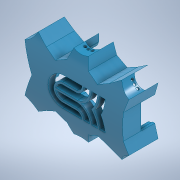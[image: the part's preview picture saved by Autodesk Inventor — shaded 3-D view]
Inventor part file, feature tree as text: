
AUTODESK INVENTOR PART (.ipt)
format: ipt  version: 2020 (Build 240168000, 168)  size: 3,561,472 bytes
history: native  units: mm
features: projected_geometry x120, extrude x44, sketch x44, reference x22, other x20, chamfer x7, hole x3, plane x2
ambient origin geometry x8: Origin, YZ Plane, XZ Plane, XY Plane, X Axis, Y Axis, Z Axis, Center Point
bodies: Solid1 (feature_tree)
feature tree (262):
  extrude  "Extrusion1"  Depth=4.404mm
  extrude  "Extrusion2"  Depth=22.0mm
  extrude  "Extrusion3"  Depth=35.3mm
  hole  "Hole2"  [1 undecoded]
  extrude  "Extrusion10"  Depth=19.0mm
  extrude  "Extrusion15"  Depth=10.0mm
  extrude  "Extrusion17"  Depth=100.0mm
  sketch  "Sketch27"  dims[d14=30.0mm d15=17.453293mm]
  hole  "Hole4"  [1 undecoded]
  extrude  "Extrusion27"  Depth=13.962634mm
  extrude  "Extrusion29"  Depth=4.8mm
  extrude  "Extrusion30"  Depth=6.2mm
  extrude  "Extrusion31"  Depth=2.5mm
  extrude  "Extrusion34"  Depth=2.5mm
  extrude  "Extrusion35"  Depth=2.0mm
  sketch  "Sketch37"  dims[d28=90.0deg d29=6.2mm]
  extrude  "Extrusion36"  Depth=6.2mm
  extrude  "Extrusion37"  Depth=33.0mm
  extrude  "Extrusion38"  Depth=2.5mm
  extrude  "Extrusion39"  Depth=4.8mm
  extrude  "Extrusion40"  Depth=6.2mm
  extrude  "Extrusion41"  Depth=2.5mm
  plane  "Work Plane1"
  extrude  "Extrusion42"  Depth=2.5mm
  hole  "Hole6"  [1 undecoded]
  extrude  "Extrusion43"  Depth=19.402mm
  chamfer  "Chamfer12"  Distance=10.0mm
  extrude  "Extrusion46"  Depth=113.583126mm
  extrude  "Extrusion47"  Depth=235.691804mm
  extrude  "Extrusion48"  Depth=12.4mm
  extrude  "Extrusion49"  Depth=12.4mm
  extrude  "Extrusion50"  Depth=142.600153mm
  extrude  "Extrusion51"  Depth=142.600153mm
  extrude  "Extrusion52"  Depth=35.0mm TaperAngle=0.0deg
  chamfer  "Chamfer13"  Distance=5.0mm
  chamfer  "Chamfer14"  Distance=22.5mm
  chamfer  "Chamfer15"  Distance=45.0mm
  chamfer  "Chamfer16"  Distance=25.0mm
  chamfer  "Chamfer17"  Distance=4.3mm
  chamfer  "Chamfer18"  Distance=9.0mm
  extrude  "Extrusion53"  Depth=35.0mm
  extrude  "Extrusion54"  Depth=35.0mm
  extrude  "Extrusion55"  Depth=35.0mm
  extrude  "Extrusion56"  Depth=35.0mm
  plane  "Work Plane2"
  extrude  "Extrusion57"  Depth=35.0mm
  extrude  "Extrusion58"  Depth=35.0mm TaperAngle=0.0deg
  extrude  "Extrusion59"  Depth=35.0mm
  extrude  "Extrusion60"  Depth=35.0mm
  extrude  "Extrusion61"  Depth=35.0mm
  extrude  "Extrusion62"  Depth=35.0mm
  extrude  "Extrusion66"  Depth=35.0mm
  extrude  "Extrusion67"  Depth=35.0mm
  extrude  "Extrusion68"  Depth=35.0mm
  extrude  "Extrusion69"  Depth=35.0mm
  extrude  "Extrusion70"  Depth=35.0mm
  extrude  "Extrusion71"  Depth=35.0mm
  extrude  "Extrusion72"  Depth=35.0mm
  sketch  "Sketch1"  dims[d0=50.0mm d1=4.404mm]
  reference  "Reference1"
  reference  "Reference2"
  reference  "Reference3"
  reference  "Reference4"
  sketch  "Sketch2"  dims[d2=135.0deg d3=22.0mm]
  reference  "Reference5"
  reference  "Reference6"
  reference  "Reference7"
  reference  "Reference8"
  reference  "Reference9"
  reference  "Reference10"
  reference  "Reference11"
  reference  "Reference12"
  reference  "Reference13"
  reference  "Reference14"
  reference  "Reference15"
  reference  "Reference16"
  sketch  "Sketch3"  dims[d4=35.3mm d5=35.3mm]
  projected_geometry  "Projected Loop1"
  projected_geometry  "Projected Loop2"
  sketch  "Sketch6"  dims[d6=98.287843mm d7=10.0mm]
  reference  "Reference23"
  reference  "Reference24"
  reference  "Reference25"
  reference  "Reference26"
  reference  "Reference27"
  reference  "Reference28"
  sketch  "Sketch13"  dims[d8=19.0mm d9=19.0mm]
  sketch  "Sketch16"  dims[d10=6.0mm d11=10.0mm]
  sketch  "Sketch18"  dims[d12=19.0mm d13=100.0mm]
  projected_geometry  "Projected Loop13"
  projected_geometry  "Projected Loop19"
  projected_geometry  "Projected Loop23"
  projected_geometry  "Projected Loop28"
  projected_geometry  "Projected Loop29"
  projected_geometry  "Projected Loop30"
  sketch  "Sketch28"  dims[d16=30.0mm d17=13.962634mm]
  projected_geometry  "Projected Loop31"
  sketch  "Sketch30"  dims[d18=2.0mm d19=4.8mm]
  projected_geometry  "Projected Loop33"
  sketch  "Sketch31"  dims[d20=6.2mm d21=6.2mm]
  projected_geometry  "Projected Loop34"
  sketch  "Sketch32"  dims[d22=33.0mm d23=2.5mm]
  projected_geometry  "Projected Loop35"
  projected_geometry  "Projected Loop36"
  projected_geometry  "Projected Loop37"
  projected_geometry  "Projected Loop38"
  projected_geometry  "Projected Loop39"
  projected_geometry  "Projected Loop40"
  projected_geometry  "Projected Loop41"
  projected_geometry  "Projected Loop42"
  projected_geometry  "Projected Loop43"
  projected_geometry  "Projected Loop44"
  projected_geometry  "Projected Loop45"
  projected_geometry  "Projected Loop46"
  sketch  "Sketch35"  dims[d24=2.0mm d25=2.5mm]
  projected_geometry  "Projected Loop52"
  sketch  "Sketch36"  dims[d26=2.0mm d27=2.0mm]
  projected_geometry  "Projected Loop53"
  projected_geometry  "Projected Loop54"
  projected_geometry  "Projected Loop55"
  projected_geometry  "Projected Loop56"
  projected_geometry  "Projected Loop57"
  sketch  "Sketch38"  dims[d30=6.2mm d31=33.0mm]
  projected_geometry  "Projected Loop58"
  sketch  "Sketch40"  dims[d32=2.0mm d33=2.5mm]
  projected_geometry  "Projected Loop59"
  sketch  "Sketch41"  dims[d35=2.0mm d36=4.8mm]
  projected_geometry  "Projected Loop60"
  sketch  "Sketch42"  dims[d37=6.2mm d38=6.2mm]
  projected_geometry  "Projected Loop61"
  projected_geometry  "Projected Loop62"
  sketch  "Sketch43"  dims[d39=33.0mm d40=2.5mm]
  projected_geometry  "Projected Loop63"
  sketch  "Sketch46"  dims[d41=2.0mm d42=2.5mm]
  sketch  "Sketch47"  dims[d43=2.0mm d44=2.0mm]
  projected_geometry  "Projected Loop67"
  sketch  "Sketch48"  dims[d45=2.5mm d46=19.402mm]
  projected_geometry  "Projected Loop68"
  sketch  "Sketch49"  dims[d47=169.440339mm]
  projected_geometry  "Projected Loop69"
  sketch  "Sketch50"  dims[d48=155.440339mm]
  projected_geometry  "Projected Loop70"
  sketch  "Sketch51"  dims[d58=2.0mm]
  projected_geometry  "Projected Loop71"
  sketch  "Sketch52"  dims[d59=2.0mm]
  projected_geometry  "Projected Loop72"
  sketch  "Sketch53"  dims[d71=4.8mm]
  projected_geometry  "Projected Loop73"
  sketch  "Sketch54"  dims[d72=33.0mm]
  sketch  "Sketch55"  dims[d73=2.5mm]
  projected_geometry  "Projected Loop74"
  sketch  "Sketch56"  dims[d74=2.0mm]
  projected_geometry  "Projected Loop75"
  projected_geometry  "Projected Loop76"
  projected_geometry  "Projected Loop77"
  projected_geometry  "Projected Loop78"
  projected_geometry  "Projected Loop79"
  projected_geometry  "Projected Loop80"
  sketch  "Sketch58"  dims[d75=2.5mm]
  sketch  "Sketch61"  dims[d76=2.0mm]
  projected_geometry  "Projected Loop91"
  projected_geometry  "Projected Loop92"
  sketch  "Sketch62"  dims[d77=14.0mm]
  projected_geometry  "Projected Loop93"
  sketch  "Sketch63"  dims[d78=2.0mm]
  projected_geometry  "Projected Loop94"
  projected_geometry  "Projected Loop95"
  projected_geometry  "Projected Loop96"
  projected_geometry  "Projected Loop97"
  projected_geometry  "Projected Loop98"
  projected_geometry  "Projected Loop99"
  projected_geometry  "Projected Loop100"
  projected_geometry  "Projected Loop101"
  projected_geometry  "Projected Loop102"
  projected_geometry  "Projected Loop103"
  projected_geometry  "Projected Loop104"
  projected_geometry  "Projected Loop105"
  projected_geometry  "Projected Loop106"
  projected_geometry  "Projected Loop107"
  projected_geometry  "Projected Loop108"
  projected_geometry  "Projected Loop109"
  projected_geometry  "Projected Loop110"
  projected_geometry  "Projected Loop111"
  projected_geometry  "Projected Loop112"
  projected_geometry  "Projected Loop113"
  projected_geometry  "Projected Loop114"
  projected_geometry  "Projected Loop115"
  projected_geometry  "Projected Loop116"
  projected_geometry  "Projected Loop117"
  projected_geometry  "Projected Loop118"
  projected_geometry  "Projected Loop119"
  projected_geometry  "Projected Loop120"
  projected_geometry  "Projected Loop121"
  projected_geometry  "Projected Loop122"
  projected_geometry  "Projected Loop123"
  projected_geometry  "Projected Loop124"
  projected_geometry  "Projected Loop125"
  projected_geometry  "Projected Loop126"
  projected_geometry  "Projected Loop127"
  projected_geometry  "Projected Loop128"
  projected_geometry  "Projected Loop129"
  projected_geometry  "Projected Loop130"
  projected_geometry  "Projected Loop131"
  projected_geometry  "Projected Loop132"
  projected_geometry  "Projected Loop133"
  projected_geometry  "Projected Loop134"
  projected_geometry  "Projected Loop135"
  projected_geometry  "Projected Loop136"
  projected_geometry  "Projected Loop137"
  projected_geometry  "Projected Loop138"
  projected_geometry  "Projected Loop139"
  projected_geometry  "Projected Loop140"
  projected_geometry  "Projected Loop141"
  projected_geometry  "Projected Loop142"
  projected_geometry  "Projected Loop143"
  projected_geometry  "Projected Loop144"
  projected_geometry  "Projected Loop145"
  projected_geometry  "Projected Loop146"
  projected_geometry  "Projected Loop147"
  sketch  "Sketch66"  dims[d79=106.731156mm]
  sketch  "Sketch67"  dims[d80=94.331156mm d81=10.0mm d82=0.0mm]
  projected_geometry  "Projected Loop149"
  sketch  "Sketch71"  dims[d83=146.583126mm d84=113.583126mm]
  projected_geometry  "Projected Loop158"
  sketch  "Sketch72"  dims[d85=207.691804mm d86=235.691804mm]
  projected_geometry  "Projected Loop159"
  sketch  "Sketch73"  dims[d87=89.108678mm d88=12.4mm]
  projected_geometry  "Projected Loop160"
  sketch  "Sketch74"  dims[d89=56.108678mm d90=12.4mm]
  projected_geometry  "Projected Loop161"
  sketch  "Sketch75"  dims[d91=23.0mm d92=142.600153mm]
  projected_geometry  "Projected Loop162"
  sketch  "Sketch76"  dims[d93=170.600153mm d94=142.600153mm]
  projected_geometry  "Projected Loop163"
  sketch  "Sketch77"  dims[d95=19.0mm d96=0.0mm d97=5.0mm d98=0.0mm d153=10.0mm d154=6.0mm d155=4.0mm d156=2.0mm d157=90.0deg d158=3.8mm d159=0.0mm d207=5.0mm d208=22.5mm d209=45.0mm d210=25.0mm d211=0.0mm d253=2.5mm d254=20.0mm d255=9.0mm d256=10.0mm d257=16.0mm d258=27.0mm d259=16.0mm d260=0.3mm d261=0.3mm d262=1.5mm d263=1.5mm d264=2.0mm d265=1.5mm d266=1.5mm d267=2.0mm d268=1.5mm d269=1.5mm d270=2.0mm d271=1.5mm d272=1.5mm d273=2.0mm d274=10.5mm d275=1.75mm d276=3.5mm d277=180.0deg d278=7.0mm d279=0.3mm d280=0.3mm d281=0.3mm d282=0.3mm d283=1.0mm d284=4.3mm d285=0.0mm d310=9.0mm d311=0.0mm d382=3.0mm d383=6.0mm d384=4.0mm d385=2.0mm d386=90.0deg d387=24.0mm d388=0.0mm d396=3.2505mm d397=3.2505mm d398=3.2505mm d400=3.2505mm d401=3.2505mm d402=2.4mm d403=0.0mm d416=3.1mm d455=6.0mm d456=4.5mm d457=4.5mm d458=1.7mm d459=12.4mm d460=6.0mm d461=4.5mm d462=4.5mm d463=6.0mm d464=4.5mm d465=4.5mm d466=6.0mm d467=4.5mm d468=4.5mm d472=6.0mm d473=4.5mm d474=4.5mm d475=4.5mm d476=4.5mm d477=6.0mm d478=154.585126mm d479=147.583126mm d480=147.583126mm d481=9.0mm d482=0.0mm d483=154.585126mm d484=90.108678mm d485=10.7mm d486=147.583126mm d487=66.300077mm d488=72.372447mm d489=10.0mm d490=0.0mm d491=0.0mm d492=231.691804mm d493=91.808678mm d494=139.883126mm d495=171.600153mm d496=1.7mm d497=5.0mm d498=0.0mm d523=88.2mm d524=34.2mm d525=17.1mm d526=44.1mm d527=5.0mm d528=5.0mm d529=10.0mm d530=0.0mm d531=54.9mm d532=27.9mm d533=13.95mm d534=27.45mm d535=2.05mm d536=2.05mm d537=6.0mm d538=6.0mm d539=6.0mm d540=6.0mm d541=10.0mm d542=25.0mm d543=0.0mm d544=18.9mm d545=6.0mm d546=18.9mm d547=6.0mm d548=18.9mm d549=6.0mm d550=18.9mm d551=10.0mm d552=0.0mm d553=48.2mm d554=11.9mm d555=2.5mm d556=1.3mm d557=23.8mm d558=20.0mm d559=0.0mm d560=3.1mm d561=3.1mm d562=3.1mm d563=3.1mm d564=2.4mm d565=0.0mm d566=3.0mm d567=3.0mm d568=3.0mm d569=3.0mm d570=3.0mm d571=3.0mm d572=3.0mm d575=3.0mm d576=3.0mm d577=3.0mm d578=100.0mm d579=0.0mm d580=3.1mm d581=3.1mm d582=3.1mm d583=3.1mm d584=2.4mm d585=0.0mm d586=0.15mm d587=0.15mm d588=20.0mm d589=0.0mm d590=8.0mm d591=0.0mm d592=3.0mm d593=6.0mm d594=4.0mm d595=2.0mm d596=90.0deg d597=6.5mm d598=0.0mm d599=15.0mm d600=15.0mm d602=15.0mm d603=15.0mm d605=15.0mm d606=90.0deg d607=90.0deg d608=90.0deg d609=90.0deg d611=15.0mm d612=6.575mm d616=6.575mm d618=90.0deg d619=90.0deg d620=6.575mm d621=6.575mm d622=6.575mm d625=6.575mm d626=6.575mm d627=90.0deg d628=6.575mm d629=6.575mm d630=6.575mm d631=6.575mm d632=90.0deg d633=90.0deg d638=90.0deg d639=90.0deg d640=6.575mm d641=6.575mm d644=6.575mm d647=6.575mm d648=6.575mm d649=6.0mm d650=0.0mm d660=10.0mm d661=2.0mm d662=45.0deg d663=3.1mm d664=3.1mm d665=3.1mm d666=3.1mm d667=3.1mm d668=3.1mm d669=2.4mm d670=0.0mm d671=9.15mm d672=4.0mm d673=6.0mm d674=0.0mm d675=4.0mm d676=9.15mm d677=6.0mm d678=0.0mm d679=4.0mm d680=9.15mm d681=6.0mm d682=0.0mm d683=6.575mm d684=6.575mm d685=19.777mm d686=4.0mm d687=9.15mm d688=10.0mm d689=0.0mm d690=4.0mm d691=9.15mm d692=10.0mm d693=0.0mm d694=10.0mm d695=0.0mm d696=4.75mm d697=10.0mm d698=45.0deg d699=4.75mm d700=10.0mm d701=45.0deg d702=4.75mm d703=10.0mm d704=45.0deg d705=4.75mm d706=10.0mm d707=45.0deg d708=4.75mm d709=10.0mm d710=45.0deg d711=4.75mm d712=10.0mm d713=45.0deg d714=4.0mm d715=10.0mm d716=0.0mm d717=0.15mm d718=10.25mm d719=0.0mm d720=4.0mm d722=4.0mm d724=4.0mm d725=4.0mm d726=4.0mm d728=4.0mm d729=4.0mm d731=4.0mm d732=4.0mm d733=4.0mm d734=4.0mm d736=4.0mm d737=4.0mm d738=4.0mm d739=4.0mm d740=4.0mm d741=4.0mm d742=4.0mm d743=4.0mm d744=4.0mm d745=4.0mm d746=5.0mm d747=15.0mm d748=15.0mm d749=90.0deg d750=8.0mm d751=8.0mm d752=8.0mm d753=8.0mm d754=10.0mm d755=0.0mm d756=20.0mm d757=0.0mm d758=180.0mm d759=204.5mm d760=0.0mm d761=208.25mm d762=0.0mm d763=0.0mm d764=0.0mm d765=84.0mm d766=0.0mm d767=129.0mm d768=529.75mm d769=0.0mm d770=19.0mm d771=0.0mm d833=10.5mm d834=10.5mm d835=3.6mm d836=10.5mm d837=3.6mm d838=35.0mm d839=3.59304mm d842=10.5mm d843=10.5mm d844=3.6mm d845=10.5mm d846=3.6mm d847=35.0mm d848=3.6mm d849=26.0mm d850=26.0mm d851=26.0mm d882=34.504mm d883=34.504271mm d884=45.284803mm d886=46.252582mm d896=72.250554mm d900=81.146242mm d901=98.942493mm d902=26.0mm d905=14.149611mm d907=92.5mm d908=0.0mm d911=10.095153mm d912=10.073861mm d913=15.839927mm d914=26.42798mm d915=12.788763mm d916=12.980494mm d917=53.526116mm d918=51.803568mm d919=9.505874mm d920=23.453824mm d921=26.856384mm d922=12.707718mm d923=9.12031mm d924=26.711334mm d925=26.711334mm d926=40.595931mm d927=22.803265mm d928=12.332518mm d929=39.875175mm d930=39.875175mm d931=36.277206mm d932=36.277206mm d933=35.156225mm d934=15.704672mm d935=69.291288mm d936=55.303053mm d937=51.773727mm d938=79.855853mm d939=41.284865mm d940=94.036504mm d941=41.284865mm d942=94.036504mm d943=41.284865mm d944=16.935641mm d945=45.291763mm d946=46.201133mm d947=69.068529mm d948=70.807052mm d949=70.97874mm d950=71.172685mm d951=71.312274mm d952=71.312274mm d953=71.519323mm d954=71.64733mm d955=72.250554mm d956=72.252582mm d957=72.252582mm d958=43.090916mm d959=84.958842mm d960=100.637635mm d961=100.637635mm d962=100.637635mm d963=65.681277mm d964=105.110496mm d965=117.226012mm d966=25.0mm d967=10.0mm d968=0.0mm d999=29.189217mm d1000=29.189217mm d1001=29.189217mm d1002=17.7mm d1003=0.0mm d1004=54.6mm d1005=72.3mm d1006=63.45mm d1007=5.0mm d1008=5.0mm d1009=5.0mm d1010=8.75mm d1011=0.0mm d1012=54.6mm d1013=72.3mm d1014=63.45mm d1015=5.0mm d1016=5.0mm d1017=5.0mm d1018=90.0deg d1019=90.0deg d1020=90.0deg d1021=45.0mm d1022=6.601mm d1023=13.202mm d1024=121.803694mm d1025=10.0mm d1026=13.202mm d1027=27.0mm d1028=0.0mm d1029=54.6mm d1030=72.3mm d1031=63.45mm d1032=5.0mm d1033=5.0mm d1034=5.0mm d1035=44.0mm d1036=0.0mm d1037=54.6mm d1038=72.3mm d1039=63.45mm d1040=5.0mm d1041=5.0mm d1042=5.0mm d1043=44.0mm d1044=0.0mm d1045=54.6mm d1046=72.3mm d1047=63.45mm d1048=5.0mm d1049=5.0mm d1050=5.0mm d1051=44.0mm d1052=0.0mm d1056=35.0mm d1057=35.0mm d1058=35.0mm d1059=35.0mm d1060=35.0mm d1061=35.0mm d1062=257.25mm d1063=0.0mm d99=0.5mm d100=0.872665mm d160=0.5mm d161=0.872665mm d162=0.5mm d163=0.872665mm d171=0.5mm d172=0.872665mm d173=0.5mm d174=0.872665mm d191=0.5mm d192=0.872665mm d193=0.5mm d194=0.872665mm d205=0.5mm d206=0.872665mm d244=0.5mm d245=0.872665mm d246=0.5mm d247=0.872665mm d307=0.5mm d308=0.872665mm d309=0.5mm d352=0.5mm d353=0.872665mm d354=0.5mm d355=0.872665mm d412=0.5mm d413=0.872665mm d414=0.5mm d415=0.872665mm d417=0.872665mm d721=0.872665mm d723=0.872665mm d1064=0.5mm d1065=0.872665mm]
  projected_geometry  "Projected Loop164"
  projected_geometry  "Projected Loop165"
  projected_geometry  "Projected Loop166"
  projected_geometry  "Projected Loop167"
  projected_geometry  "Projected Loop168"
  projected_geometry  "Projected Loop169"
  projected_geometry  "Projected Loop170"
  other  "<userpath>\Documents\Inventor Projects\SpiderTest\Test3\SpiderLegDemo.iam"
  other  "SpiderLegDemo.iam"
  other  "Tower Pro MG90S Micro servo:1"
  other  "Крышка корпуса задняя:1"
  other  "Крышка корпуса:1"
  other  "LegSup:1"
  other  "<userpath>\Documents\Inventor Projects\SpiderTest\Test5\Demo.iam"
  other  "Demo.iam"
  other  "SpiderLegDemoRight:1"
  other  "SpiderLegDemoRight:5"
  other  "<userpath>\Documents\Inventor Projects\SpiderTest\Test3\Demo.iam"
  other  "SpiderLegDemo:3"
  other  "SpiderLegDemo:4"
  other  "SpiderLegDemo:2"
  other  "SpiderLegDemoRight:6"
  other  "SpiderLegDemoLeft:2"
  other  "Вал последний с чем то:1"
  other  "SpiderLegDemoLeft:3"
  other  "ограничитель:2"
  other  "SpiderLegDemoLeft:1"
note: 3 required parameter values undecoded (feature->parameter linkage not recoverable at this tier; creation-order binding heuristic only, values carry confidence <= 0.55)
